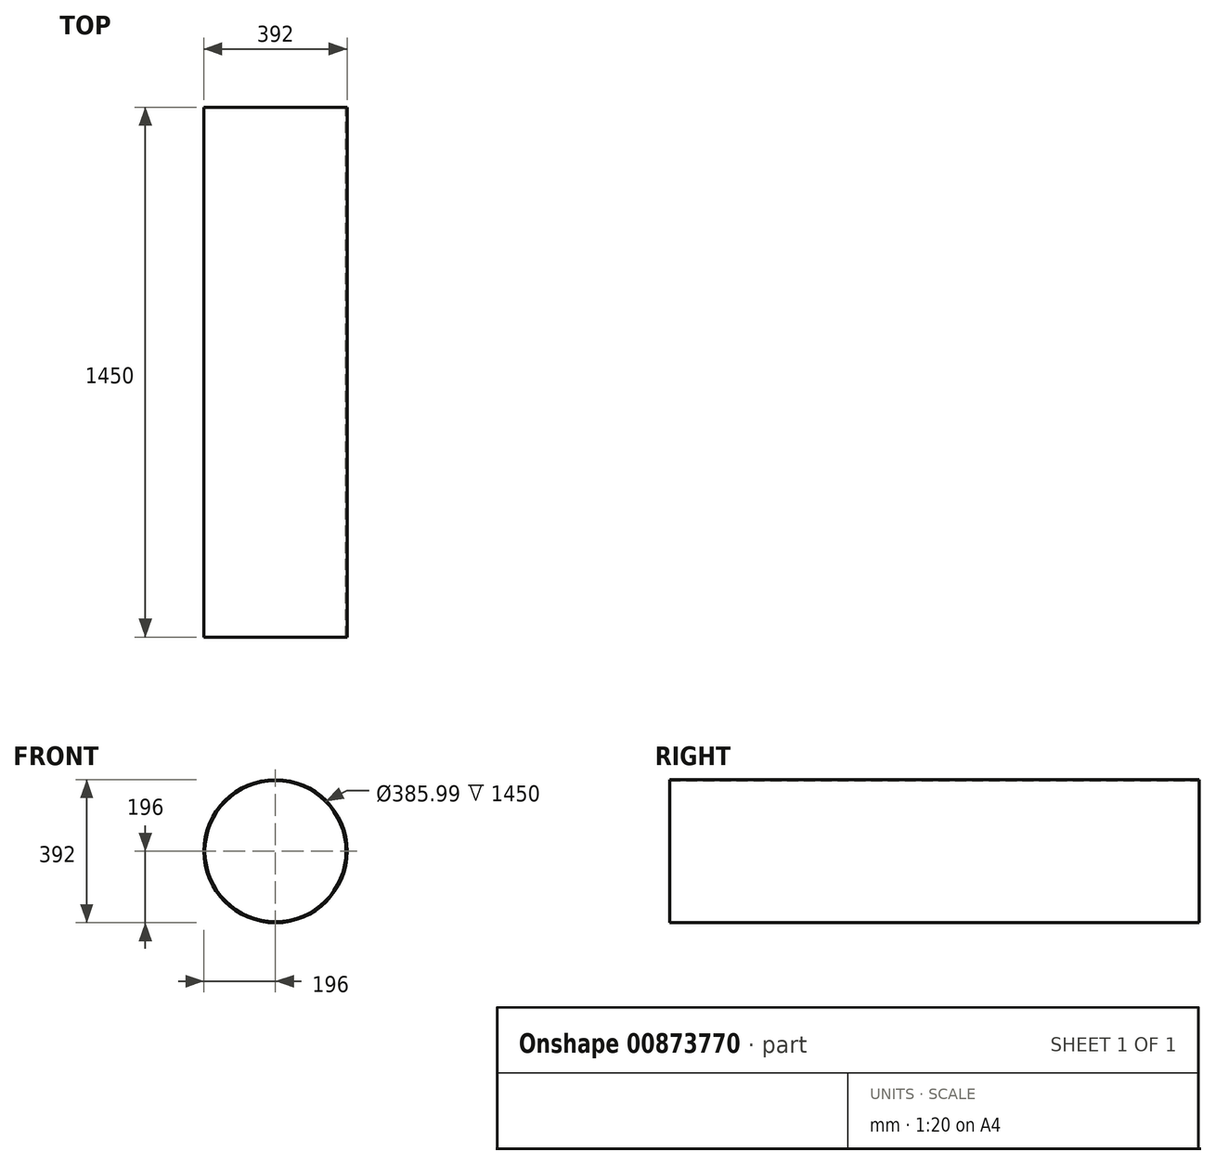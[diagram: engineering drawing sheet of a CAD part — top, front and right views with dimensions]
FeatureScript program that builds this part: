
annotation { "Feature Type Name" : "Feature", "Feature Type Description" : "" }
export const myFeature = defineFeature(function(context is Context, id is Id, definition is map)
    precondition{}
    {
        {
            var Q0;
            Q0=qCreatedBy(makeId("Front.planeOp"),FACE);
            var sketch = newSketch(context, id + "F0", { "sketchPlane" : qUnion([Q0])});
            skCircle(sketch, "E0", {"center": v(0, 0) * mm, "radius": 25 * mm});
            skSolve(sketch);
        }
        {
            var Q0;
            Q0=qCreatedBy(makeId("Front.planeOp"),FACE);
            var sketch = newSketch(context, id + "F1", { "sketchPlane" : qUnion([Q0])});
            skCircle(sketch, "E1.0", {"center": v(0, 0) * mm, "radius": 193 * mm});
            skSolve(sketch);
        }
        {
            var Q0;
            Q0=makeQuery(id+"F1.imprint","IMPRINT",FACE,{"disambiguationData":[TD([[makeQuery(id+"F1.imprint","IMPRINT",EDGE,{"derivedFrom":sQuery(id+"F1.wireOp",EDGE,"E1.0")}),1.0]])]});
            var Q1;
            Q1=sQuery(id+"F0.wireOp",EDGE,"E0");
            extrude(context, id + "F2", {"entities" : qUnion([Q0]), "surfaceEntities" : qUnion([Q1]), "endBound" : BoundingType.SYMMETRIC, "depth" : 1450 * mm, "offsetDistance" : 25.4 * mm});
        }
        {
            var Q0;
            Q0=makeQuery(id+"F2.opExtrude","CAP_FACE",FACE,{"disambiguationData":[OSD([sQuery(id+"F1.wireOp",EDGE,"E1.0")])],"isStart":false});
            var Q1;
            Q1=makeQuery(id+"F2.opExtrude","CAP_FACE",FACE,{"disambiguationData":[OSD([sQuery(id+"F1.wireOp",EDGE,"E1.0")])],"isStart":true});
            shell(context, id + "F3", {"entities" : qUnion([Q0, Q1]), "thickness" : 3 * mm, "oppositeDirection" : true});
        }
    });
